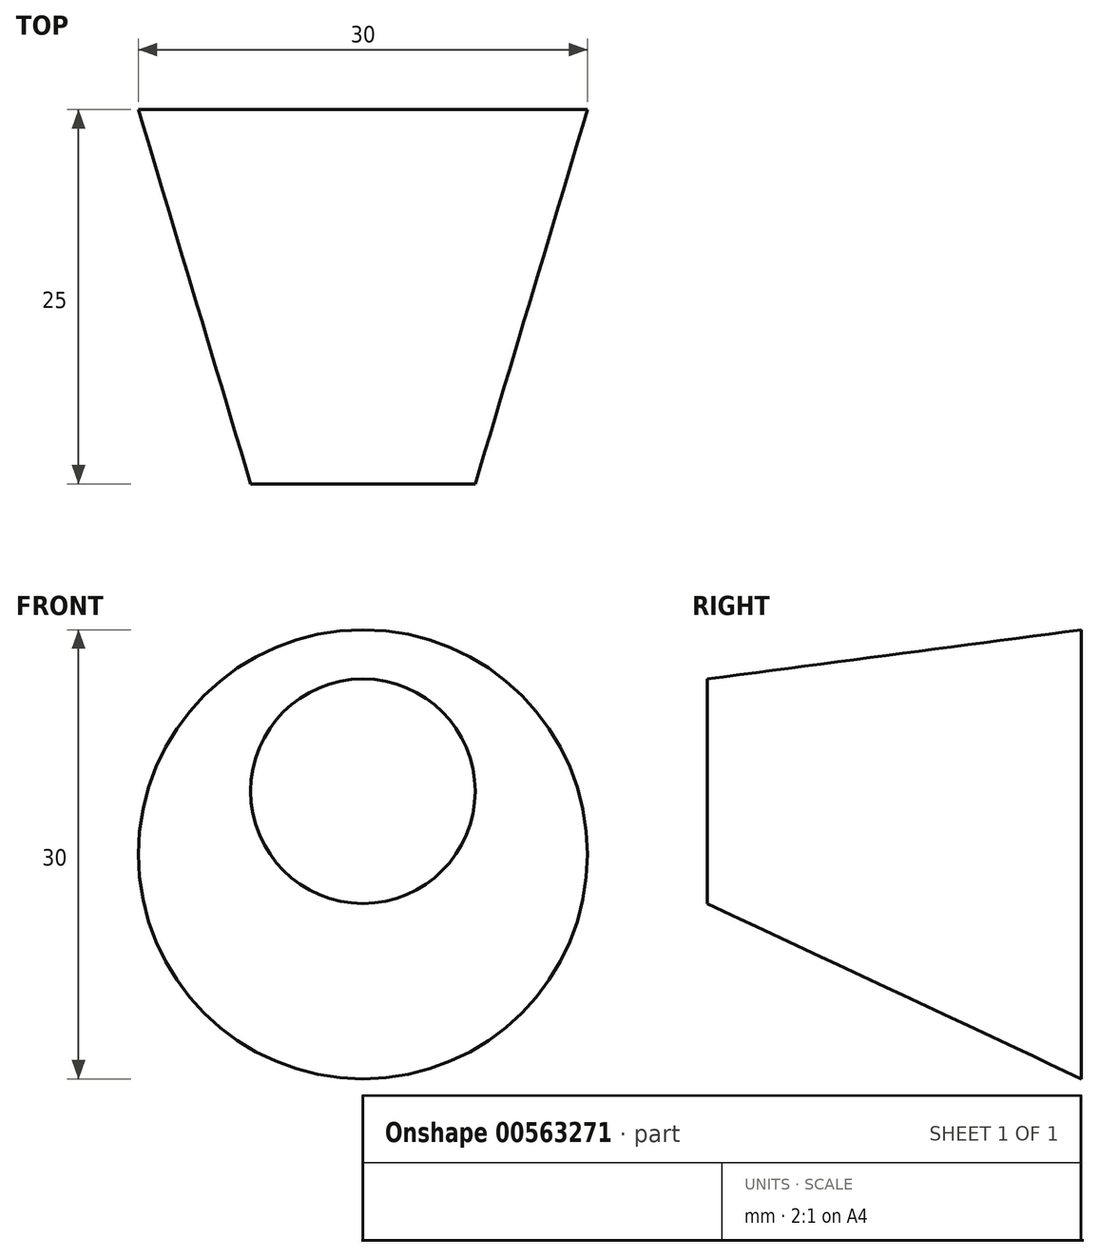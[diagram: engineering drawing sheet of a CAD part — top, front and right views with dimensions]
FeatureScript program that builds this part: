
annotation { "Feature Type Name" : "Feature", "Feature Type Description" : "" }
export const myFeature = defineFeature(function(context is Context, id is Id, definition is map)
    precondition{}
    {
        {
            var Q0;
            Q0=qCreatedBy(makeId("Front.planeOp"),FACE);
            var sketch = newSketch(context, id + "F0", { "sketchPlane" : qUnion([Q0])});
            skCircle(sketch, "E0", {"center": v(0, 0) * mm, "radius": 15 * mm});
            skSolve(sketch);
        }
        {
            var Q0;
            Q0=qCreatedBy(makeId("Front.planeOp"),FACE);
            cPlane(context, id + "F1", {"entities" : qUnion([Q0]), "cplaneType" : CPlaneType.OFFSET, "offset" : 25 * mm, "width" : 150 * mm, "height" : 150 * mm});
        }
        {
            var Q0;
            Q0=qCreatedBy(id+"F1.planeOp",FACE);
            var sketch = newSketch(context, id + "F2", { "sketchPlane" : qUnion([Q0])});
            skCircle(sketch, "E1", {"center": v(0, 4.21) * mm, "radius": 7.5 * mm});
            skSolve(sketch);
        }
        {
            var Q0;
            Q0=makeQuery(id+"F0.imprint","IMPRINT",FACE,{"disambiguationData":[TD([[makeQuery(id+"F0.imprint","IMPRINT",EDGE,{"derivedFrom":sQuery(id+"F0.wireOp",EDGE,"E0")}),1.0]])]});
            var Q1;
            Q1=makeQuery(id+"F2.imprint","IMPRINT",FACE,{"disambiguationData":[TD([[makeQuery(id+"F2.imprint","IMPRINT",EDGE,{"derivedFrom":sQuery(id+"F2.wireOp",EDGE,"E1")}),1.0]])]});
            loft(context, id + "F3", {"sheetProfilesArray" : [{ "sheetProfileEntities" : qUnion([Q0]) }, { "sheetProfileEntities" : qUnion([Q1]) }]});
        }
    });
